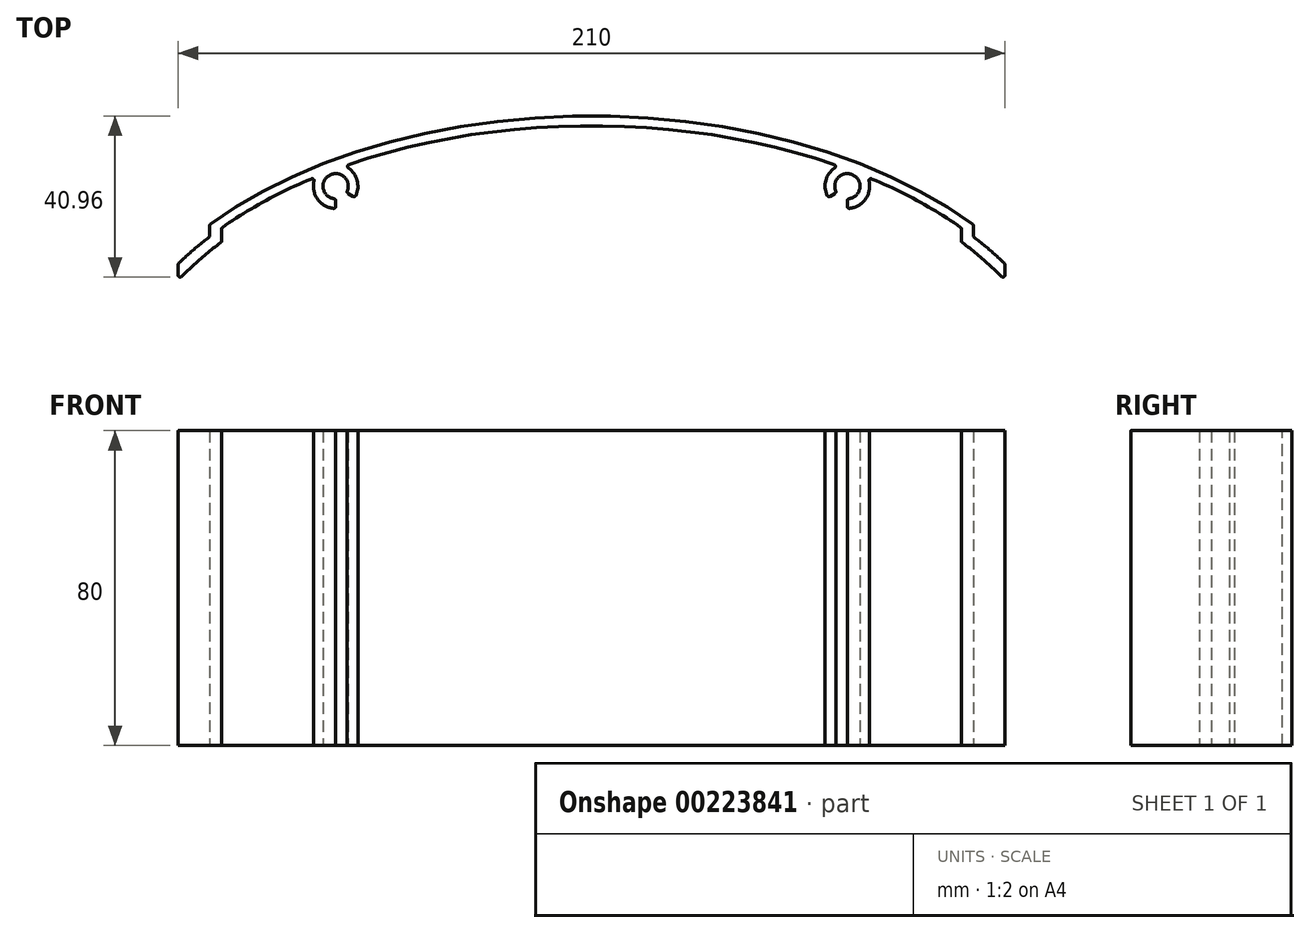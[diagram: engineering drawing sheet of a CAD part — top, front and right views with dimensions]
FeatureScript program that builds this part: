
annotation { "Feature Type Name" : "Feature", "Feature Type Description" : "" }
export const myFeature = defineFeature(function(context is Context, id is Id, definition is map)
    precondition{}
    {
        {
            var Q0;
            Q0=qCreatedBy(makeId("Top.planeOp"), FACE);
            var sketch = newSketch(context, id + "F0", { "sketchPlane" : qUnion([Q0])});
            skLineSegment(sketch, "E0", {"start": v(-156.64, 0) * mm, "end": v(169.1, 0) * mm, "construction": true});
            skLineSegment(sketch, "E1", {"start": v(0, 0) * mm, "end": v(0, 75.15) * mm, "construction": true});
            skArc(sketch, "E2", {"start": v(-62.04, 56.09) * mm, "mid": v(-66.6, 60.07) * mm, "end": v(-65.43, 54.13) * mm});
            skArc(sketch, "E3.0", {"start": v(-70.5, 58.6) * mm, "mid": v(-69.6, 54.01) * mm, "end": v(-65.55, 51.68) * mm});
            skArc(sketch, "E4.MirrorC", {"start": v(70.5, 58.6) * mm, "mid": v(69.6, 54.01) * mm, "end": v(65.55, 51.68) * mm});
            skArc(sketch, "E5.MirrorC", {"start": v(62.04, 56.09) * mm, "mid": v(66.6, 60.07) * mm, "end": v(65.43, 54.13) * mm});
            skLineSegment(sketch, "E6.0", {"start": v(105, 34.69) * mm, "end": v(105, 37.38) * mm});
            skLineSegment(sketch, "E7.0", {"start": v(-105, 34.69) * mm, "end": v(-105, 37.38) * mm});
            skEllipticalArc(sketch, "E8.trimOffspring", {});
            skEllipticalArc(sketch, "E9.trimOffspring", {});
            skEllipticalArc(sketch, "E10.trimOffspring", {});
            skEllipticalArc(sketch, "E11.trimOffspring", {});
            skEllipticalArc(sketch, "E12.trimOffspring", {});
            skEllipticalArc(sketch, "E13.trimOffspring", {});
            skLineSegment(sketch, "E14.0", {"start": v(94, 43.37) * mm, "end": v(94, 46.43) * mm});
            skLineSegment(sketch, "E15.0", {"start": v(-94, 43.37) * mm, "end": v(-94, 46.43) * mm});
            skLineSegment(sketch, "E16.0", {"start": v(-97, 44.74) * mm, "end": v(-97, 47.26) * mm});
            skLineSegment(sketch, "E17.0", {"start": v(97, 44.74) * mm, "end": v(97, 47.26) * mm});
            skEllipticalArc(sketch, "E18.trimOffspring", {});
            skEllipticalArc(sketch, "E19.trimOffspring", {});
            skLineSegment(sketch, "E20", {"start": v(65, 53.63) * mm, "end": v(65, 52.17) * mm});
            skLineSegment(sketch, "E21", {"start": v(61.83, 55.47) * mm, "end": v(60.56, 54.74) * mm});
            skArc(sketch, "E22.trimOffspring", {"start": v(59.86, 54.96) * mm, "mid": v(59.55, 58.8) * mm, "end": v(61.77, 61.93) * mm});
            skLineSegment(sketch, "E23", {"start": v(-65, 53.63) * mm, "end": v(-65, 52.17) * mm});
            skLineSegment(sketch, "E24", {"start": v(-61.83, 55.47) * mm, "end": v(-60.56, 54.74) * mm});
            skArc(sketch, "E25.trimOffspring", {"start": v(-59.86, 54.96) * mm, "mid": v(-59.55, 58.8) * mm, "end": v(-61.77, 61.93) * mm});
            skPoint(sketch, "E26.visualSharp", {"position": v(-105, 37.59) * mm});
            skArc(sketch, "E26.filletArc", {"start": v(-104.85, 37.74) * mm, "mid": v(-104.96, 37.57) * mm, "end": v(-105, 37.38) * mm});
            skPoint(sketch, "E27.visualSharp", {"position": v(-105, 33.44) * mm});
            skArc(sketch, "E27.filletArc", {"start": v(-105, 34.69) * mm, "mid": v(-104.69, 34.22) * mm, "end": v(-104.14, 34.34) * mm});
            skPoint(sketch, "E28.visualSharp", {"position": v(-94, 43.12) * mm});
            skArc(sketch, "E28.filletArc", {"start": v(-94.2, 42.97) * mm, "mid": v(-94.05, 43.15) * mm, "end": v(-94, 43.37) * mm});
            skPoint(sketch, "E29.visualSharp", {"position": v(-97, 44.5) * mm});
            skArc(sketch, "E29.filletArc", {"start": v(-97.2, 44.34) * mm, "mid": v(-97.05, 44.52) * mm, "end": v(-97, 44.74) * mm});
            skPoint(sketch, "E30.visualSharp", {"position": v(-97, 47.51) * mm});
            skArc(sketch, "E30.filletArc", {"start": v(-96.8, 47.66) * mm, "mid": v(-96.95, 47.49) * mm, "end": v(-97, 47.26) * mm});
            skPoint(sketch, "E31.visualSharp", {"position": v(-94, 46.7) * mm});
            skArc(sketch, "E31.filletArc", {"start": v(-93.79, 46.84) * mm, "mid": v(-93.94, 46.67) * mm, "end": v(-94, 46.43) * mm});
            skPoint(sketch, "E32.visualSharp", {"position": v(97, 47.51) * mm});
            skArc(sketch, "E32.filletArc", {"start": v(97, 47.26) * mm, "mid": v(96.95, 47.49) * mm, "end": v(96.8, 47.66) * mm});
            skPoint(sketch, "E33.visualSharp", {"position": v(94, 46.7) * mm});
            skArc(sketch, "E33.filletArc", {"start": v(94, 46.43) * mm, "mid": v(93.94, 46.67) * mm, "end": v(93.79, 46.84) * mm});
            skPoint(sketch, "E34.visualSharp", {"position": v(97, 44.5) * mm});
            skArc(sketch, "E34.filletArc", {"start": v(97, 44.74) * mm, "mid": v(97.05, 44.52) * mm, "end": v(97.2, 44.34) * mm});
            skPoint(sketch, "E35.visualSharp", {"position": v(94, 43.12) * mm});
            skArc(sketch, "E35.filletArc", {"start": v(94, 43.37) * mm, "mid": v(94.05, 43.15) * mm, "end": v(94.2, 42.97) * mm});
            skPoint(sketch, "E36.visualSharp", {"position": v(105, 37.59) * mm});
            skArc(sketch, "E36.filletArc", {"start": v(105, 37.38) * mm, "mid": v(104.96, 37.57) * mm, "end": v(104.85, 37.74) * mm});
            skPoint(sketch, "E37.visualSharp", {"position": v(105, 33.44) * mm});
            skArc(sketch, "E37.filletArc", {"start": v(104.14, 34.34) * mm, "mid": v(104.69, 34.22) * mm, "end": v(105, 34.69) * mm});
            skPoint(sketch, "E38.visualSharp", {"position": v(62.68, 62.45) * mm});
            skArc(sketch, "E38.filletArc", {"start": v(61.77, 61.93) * mm, "mid": v(61.98, 62.41) * mm, "end": v(61.64, 62.82) * mm});
            skPoint(sketch, "E39.visualSharp", {"position": v(70.16, 59.6) * mm});
            skArc(sketch, "E39.filletArc", {"start": v(71.18, 59.18) * mm, "mid": v(70.66, 59.1) * mm, "end": v(70.5, 58.6) * mm});
            skPoint(sketch, "E40.visualSharp", {"position": v(62.23, 55.7) * mm});
            skArc(sketch, "E40.filletArc", {"start": v(61.83, 55.47) * mm, "mid": v(62.05, 55.74) * mm, "end": v(62.04, 56.09) * mm});
            skPoint(sketch, "E41.visualSharp", {"position": v(60.1, 54.47) * mm});
            skArc(sketch, "E41.filletArc", {"start": v(59.86, 54.96) * mm, "mid": v(60.16, 54.7) * mm, "end": v(60.56, 54.74) * mm});
            skPoint(sketch, "E42.visualSharp", {"position": v(65, 54.1) * mm});
            skArc(sketch, "E42.filletArc", {"start": v(65.43, 54.13) * mm, "mid": v(65.12, 53.96) * mm, "end": v(65, 53.63) * mm});
            skPoint(sketch, "E43.visualSharp", {"position": v(65, 51.65) * mm});
            skArc(sketch, "E43.filletArc", {"start": v(65, 52.17) * mm, "mid": v(65.16, 51.8) * mm, "end": v(65.55, 51.68) * mm});
            skPoint(sketch, "E44.visualSharp", {"position": v(-70.16, 59.6) * mm});
            skArc(sketch, "E44.filletArc", {"start": v(-70.5, 58.6) * mm, "mid": v(-70.66, 59.1) * mm, "end": v(-71.18, 59.18) * mm});
            skPoint(sketch, "E45.visualSharp", {"position": v(-62.68, 62.45) * mm});
            skArc(sketch, "E45.filletArc", {"start": v(-61.64, 62.82) * mm, "mid": v(-61.98, 62.41) * mm, "end": v(-61.77, 61.93) * mm});
            skPoint(sketch, "E46.visualSharp", {"position": v(-62.23, 55.7) * mm});
            skArc(sketch, "E46.filletArc", {"start": v(-62.04, 56.09) * mm, "mid": v(-62.05, 55.74) * mm, "end": v(-61.83, 55.47) * mm});
            skPoint(sketch, "E47.visualSharp", {"position": v(-60.1, 54.47) * mm});
            skArc(sketch, "E47.filletArc", {"start": v(-60.56, 54.74) * mm, "mid": v(-60.16, 54.7) * mm, "end": v(-59.86, 54.96) * mm});
            skPoint(sketch, "E48.visualSharp", {"position": v(-65, 54.1) * mm});
            skArc(sketch, "E48.filletArc", {"start": v(-65, 53.63) * mm, "mid": v(-65.12, 53.96) * mm, "end": v(-65.43, 54.13) * mm});
            skPoint(sketch, "E49.visualSharp", {"position": v(-65, 51.65) * mm});
            skArc(sketch, "E49.filletArc", {"start": v(-65.55, 51.68) * mm, "mid": v(-65.16, 51.8) * mm, "end": v(-65, 52.17) * mm});
            const initialGuessF0  = {"E8.trimOffspring": [0, 0, -1, 0, 0.1252, 0.07515, 3.8286355483522434, 5.596142412417138], "E9.trimOffspring": [0, 0, -1, 0, 0.1227, 0.07265, 3.687774361426799, 3.7980848797022593], "E10.trimOffspring": [0, 0, -1, 0, 0.1197, 0.06965, 3.6571392728315035, 3.806483437829926], "E11.trimOffspring": [0, 0, -1, 0, 0.1197, 0.06965, 5.618294522939453, 5.767638687937885], "E12.trimOffspring": [0, 0, -1, 0, 0.1227, 0.07265, 4.1860288486552015, 5.238749112114178], "E13.trimOffspring": [0, 0, -1, 0, 0.1227, 0.07265, 5.3312490253623235, 5.582440696790394], "E18.trimOffspring": [0, 0, -1, 0, 0.1227, 0.07265, 5.62669308106712, 5.737003599342577], "E19.trimOffspring": [0, 0, -1, 0, 0.1227, 0.07265, 3.842337263979, 4.093528935407058]};
            skSetInitialGuess(sketch, initialGuessF0);
            skSolve(sketch);
        }
        {
            var Q0;
            Q0 = qSketchRegion(id + "F0", true);
            extrude(context, id + "F1", {"entities" : qUnion([Q0]), "depth" : 80 * mm, "offsetDistance" : 25 * mm});
        }
    });
